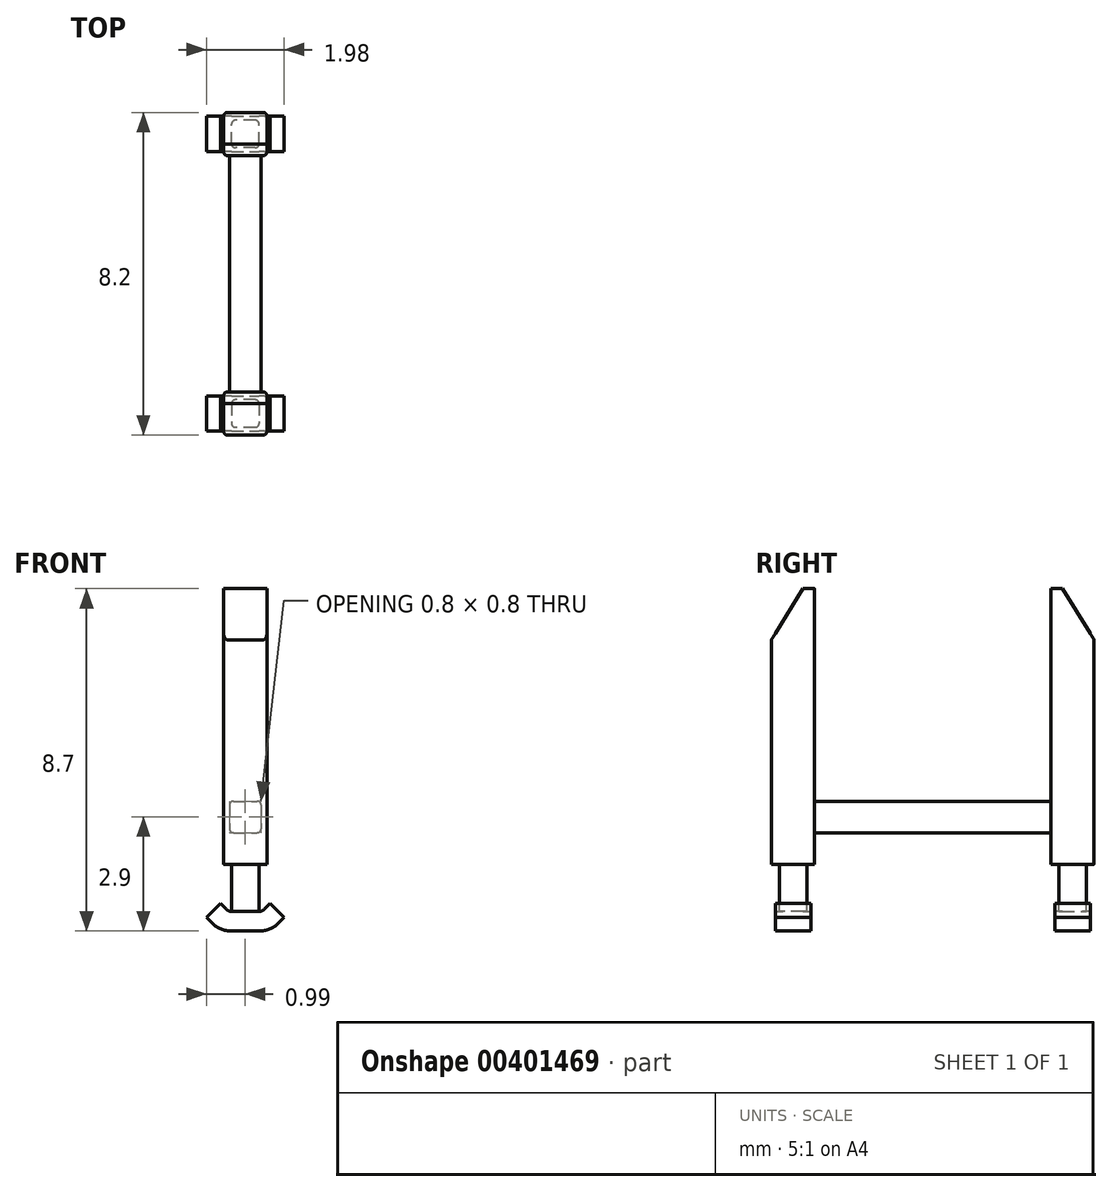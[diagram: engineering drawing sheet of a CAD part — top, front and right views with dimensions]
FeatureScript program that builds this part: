
annotation { "Feature Type Name" : "Feature", "Feature Type Description" : "" }
export const myFeature = defineFeature(function(context is Context, id is Id, definition is map)
    precondition{}
    {
        {
            var Q0;
            Q0=qCreatedBy(makeId("Right.planeOp"),FACE);
            var sketch = newSketch(context, id + "F0", { "sketchPlane" : qUnion([Q0])});
            skLineSegment(sketch, "E0", {"start": v(3, 0) * mm, "end": v(4.1, 0) * mm});
            skLineSegment(sketch, "E1", {"start": v(4.1, 0) * mm, "end": v(4.1, -7) * mm});
            skLineSegment(sketch, "E2", {"start": v(3, -7) * mm, "end": v(4.1, -7) * mm});
            skLineSegment(sketch, "E3", {"start": v(3, -7) * mm, "end": v(3, 0) * mm});
            skSolve(sketch);
        }
        {
            var Q0;
            Q0 = qSketchRegion(id + "F0", true);
            extrude(context, id + "F1", {"entities" : qUnion([Q0]), "endBound" : BoundingType.SYMMETRIC, "depth" : 1.1 * mm});
        }
        {
            var Q0;
            Q0=makeQuery(id+"F1.opExtrude","SWEPT_FACE",FACE,{"disambiguationData":[OSD([sQuery(id+"F0.wireOp",EDGE,"E2")])]});
            var sketch = newSketch(context, id + "F2", { "sketchPlane" : qUnion([Q0])});
            skLineSegment(sketch, "E4.bottom", {"start": v(0.35, -3.2) * mm, "end": v(-0.35, -3.2) * mm});
            skLineSegment(sketch, "E4.top", {"start": v(0.35, -3.9) * mm, "end": v(-0.35, -3.9) * mm});
            skLineSegment(sketch, "E4.left", {"start": v(0.35, -3.2) * mm, "end": v(0.35, -3.9) * mm});
            skLineSegment(sketch, "E4.right", {"start": v(-0.35, -3.2) * mm, "end": v(-0.35, -3.9) * mm});
            skLineSegment(sketch, "E5", {"start": v(0.55, -3.55) * mm, "end": v(0.35, -3.55) * mm, "construction": true});
            skPoint(sketch, "E5.endSnap0", {"position": v(0.35, -3.55) * mm});
            skLineSegment(sketch, "E6", {"start": v(0, -3.9) * mm, "end": v(0, -4.1) * mm, "construction": true});
            skSolve(sketch);
        }
        {
            var Q0;
            Q0 = qSketchRegion(id + "F2", true);
            extrude(context, id + "F3", {"entities" : qUnion([Q0]), "operationType" : NewBodyOperationType.ADD, "depth" : 1.2 * mm});
        }
        {
            var Q0;
            Q0=makeQuery(id+"F1.opExtrude","CAP_EDGE",EDGE,{"disambiguationData":[OSD([sQuery(id+"F0.wireOp",EDGE,"E1")])],"isStart":false});
            var Q1;
            Q1=makeQuery(id+"F1.opExtrude","CAP_EDGE",EDGE,{"disambiguationData":[OSD([sQuery(id+"F0.wireOp",EDGE,"E3")])],"isStart":false});
            var Q2;
            Q2=makeQuery(id+"F1.opExtrude","CAP_EDGE",EDGE,{"disambiguationData":[OSD([sQuery(id+"F0.wireOp",EDGE,"E1")])],"isStart":true});
            var Q3;
            Q3=makeQuery(id+"F3.opExtrude","SWEPT_EDGE",EDGE,{"disambiguationData":[OSD([sQuery(id+"F2.wireOp",EDGE,"E4.top"),sQuery(id+"F2.wireOp",EDGE,"E4.left")])]});
            var Q4;
            Q4=makeQuery(id+"F3.opExtrude","SWEPT_EDGE",EDGE,{"disambiguationData":[OSD([sQuery(id+"F2.wireOp",EDGE,"E4.top"),sQuery(id+"F2.wireOp",EDGE,"E4.right")])]});
            var Q5;
            Q5=makeQuery(id+"F3.opExtrude","SWEPT_EDGE",EDGE,{"disambiguationData":[OSD([sQuery(id+"F2.wireOp",EDGE,"E4.bottom"),sQuery(id+"F2.wireOp",EDGE,"E4.left")])]});
            var Q6;
            Q6=makeQuery(id+"F3.opExtrude","SWEPT_EDGE",EDGE,{"disambiguationData":[OSD([sQuery(id+"F2.wireOp",EDGE,"E4.bottom"),sQuery(id+"F2.wireOp",EDGE,"E4.right")])]});
            var Q7;
            Q7=makeQuery(id+"F1.opExtrude","CAP_EDGE",EDGE,{"disambiguationData":[OSD([sQuery(id+"F0.wireOp",EDGE,"E3")])],"isStart":true});
            fillet(context, id + "F4", {"entities" : qUnion([Q0, Q1, Q2, Q3, Q4, Q5, Q6, Q7]), "radius" : 0.1 * mm, "tangentPropagation" : true, "allowEdgeOverflow" : false});
        }
        {
            var Q0;
            Q0=makeQuery(id+"F3.opExtrude","SWEPT_FACE",FACE,{"disambiguationData":[OSD([sQuery(id+"F2.wireOp",EDGE,"E4.top")])]});
            var Q1;
            Q1=makeQuery(id+"F3.opExtrude","SWEPT_FACE",FACE,{"disambiguationData":[OSD([sQuery(id+"F2.wireOp",EDGE,"E4.bottom")])]});
            cPlane(context, id + "F5", {"entities" : qUnion([Q0, Q1]), "cplaneType" : CPlaneType.MID_PLANE, "offset" : 25 * mm, "width" : 150 * mm, "height" : 150 * mm});
        }
        {
            var Q0;
            Q0=qCreatedBy(id+"F5.planeOp",FACE);
            var sketch = newSketch(context, id + "F6", { "sketchPlane" : qUnion([Q0])});
            skLineSegment(sketch, "E7", {"start": v(0.35, -8.2) * mm, "end": v(-0.35, -8.2) * mm});
            skArc(sketch, "E8", {"start": v(-0.35, -8.2) * mm, "mid": v(-0.43, -8.18) * mm, "end": v(-0.5, -8.14) * mm});
            skArc(sketch, "E9", {"start": v(0.35, -8.2) * mm, "mid": v(0.43, -8.18) * mm, "end": v(0.5, -8.14) * mm});
            skLineSegment(sketch, "E10", {"start": v(0.5, -8.14) * mm, "end": v(0.63, -8) * mm});
            skLineSegment(sketch, "E11", {"start": v(0.63, -8) * mm, "end": v(0.99, -8.35) * mm});
            skLineSegment(sketch, "E12", {"start": v(0.99, -8.35) * mm, "end": v(0.84, -8.5) * mm});
            skLineSegment(sketch, "E13", {"start": v(-0.5, -8.14) * mm, "end": v(-0.63, -8) * mm});
            skLineSegment(sketch, "E14", {"start": v(-0.63, -8) * mm, "end": v(-0.99, -8.35) * mm});
            skLineSegment(sketch, "E15", {"start": v(-0.99, -8.35) * mm, "end": v(-0.84, -8.5) * mm});
            skArc(sketch, "E16", {"start": v(0.35, -8.7) * mm, "mid": v(0.62, -8.65) * mm, "end": v(0.84, -8.5) * mm});
            skLineSegment(sketch, "E17", {"start": v(0.35, -8.7) * mm, "end": v(-0.35, -8.7) * mm});
            skArc(sketch, "E18", {"start": v(-0.84, -8.5) * mm, "mid": v(-0.62, -8.65) * mm, "end": v(-0.35, -8.7) * mm});
            skPoint(sketch, "E19.orphan", {"position": v(-0.7, -8.64) * mm});
            skSolve(sketch);
        }
        {
            var Q0;
            Q0 = qSketchRegion(id + "F6", true);
            extrude(context, id + "F7", {"entities" : qUnion([Q0]), "operationType" : NewBodyOperationType.ADD, "endBound" : BoundingType.SYMMETRIC, "depth" : 0.9 * mm});
        }
        {
            var Q0;
            Q0=makeQuery(id+"F1.opExtrude","SWEPT_FACE",FACE,{"disambiguationData":[OSD([sQuery(id+"F0.wireOp",EDGE,"E3")])]});
            var sketch = newSketch(context, id + "F8", { "sketchPlane" : qUnion([Q0])});
            skLineSegment(sketch, "E20.bottom", {"start": v(-0.4, -5.4) * mm, "end": v(0.4, -5.4) * mm});
            skLineSegment(sketch, "E20.top", {"start": v(-0.4, -6.2) * mm, "end": v(0.4, -6.2) * mm});
            skLineSegment(sketch, "E20.left", {"start": v(-0.4, -5.4) * mm, "end": v(-0.4, -6.2) * mm});
            skLineSegment(sketch, "E20.right", {"start": v(0.4, -5.4) * mm, "end": v(0.4, -6.2) * mm});
            skLineSegment(sketch, "E21", {"start": v(-0.4, -5.8) * mm, "end": v(-0.45, -5.8) * mm, "construction": true});
            skLineSegment(sketch, "E22", {"start": v(0.4, -5.8) * mm, "end": v(0.45, -5.8) * mm, "construction": true});
            skSolve(sketch);
        }
        {
            var Q0;
            Q0 = qSketchRegion(id + "F8", true);
            var Q1;
            Q1=qCreatedBy(makeId("Front.planeOp"),FACE);
            extrude(context, id + "F9", {"entities" : qUnion([Q0]), "operationType" : NewBodyOperationType.ADD, "endBound" : BoundingType.UP_TO_SURFACE, "endBoundEntityFace" : qUnion([Q1]), "depth" : 25 * mm});
        }
        {
            var Q0;
            Q0=makeQuery(id+"F9.opExtrude","SWEPT_EDGE",EDGE,{"disambiguationData":[OSD([sQuery(id+"F8.wireOp",EDGE,"E20.bottom"),sQuery(id+"F8.wireOp",EDGE,"E20.left")])]});
            var Q1;
            Q1=makeQuery(id+"F9.opExtrude","SWEPT_EDGE",EDGE,{"disambiguationData":[OSD([sQuery(id+"F8.wireOp",EDGE,"E20.top"),sQuery(id+"F8.wireOp",EDGE,"E20.left")])]});
            var Q2;
            Q2=makeQuery(id+"F9.opExtrude","SWEPT_EDGE",EDGE,{"disambiguationData":[OSD([sQuery(id+"F8.wireOp",EDGE,"E20.top"),sQuery(id+"F8.wireOp",EDGE,"E20.right")])]});
            var Q3;
            Q3=makeQuery(id+"F9.opExtrude","SWEPT_EDGE",EDGE,{"disambiguationData":[OSD([sQuery(id+"F8.wireOp",EDGE,"E20.bottom"),sQuery(id+"F8.wireOp",EDGE,"E20.right")])]});
            fillet(context, id + "F10", {"entities" : qUnion([Q0, Q1, Q2, Q3]), "radius" : 0.1 * mm, "tangentPropagation" : true, "allowEdgeOverflow" : false});
        }
        {
            var Q0;
            Q0=makeQuery(id+"F1.opExtrude","SWEPT_EDGE",EDGE,{"disambiguationData":[OSD([sQuery(id+"F0.wireOp",EDGE,"E0"),sQuery(id+"F0.wireOp",EDGE,"E1")])]});
            chamfer(context, id + "F11", {"entities" : qUnion([Q0]), "chamferType" : ChamferType.TWO_OFFSETS, "width1" : 0.8 * mm, "oppositeDirection" : false, "width2" : 1.3 * mm});
        }
        {
            var Q0;
            Q0=makeQuery(id+"F1.opExtrude","SWEPT_BODY",BODY,{"disambiguationData":[OSD([sQuery(id+"F0.wireOp",EDGE,"E0"),sQuery(id+"F0.wireOp",EDGE,"E1"),sQuery(id+"F0.wireOp",EDGE,"E2"),sQuery(id+"F0.wireOp",EDGE,"E3")])]});
            var Q1;
            Q1=qCreatedBy(makeId("Front.planeOp"),FACE);
            mirror(context, id + "F12", {"operationType" : NewBodyOperationType.ADD, "entities" : qUnion([Q0]), "mirrorPlane" : qUnion([Q1])});
        }
    });
